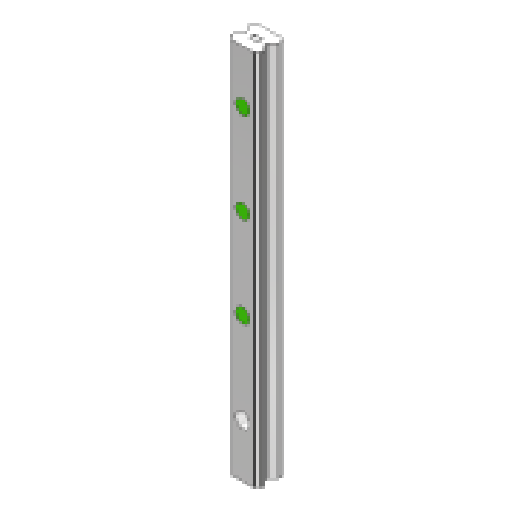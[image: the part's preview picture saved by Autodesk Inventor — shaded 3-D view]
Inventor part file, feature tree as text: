
AUTODESK INVENTOR PART (.ipt)
format: ipt  version: 2024.3 (Build 283343000, 343)  size: 185,344 bytes
history: native  units: in
note: dims shown in document units (in); Inventor stores cm internally (conversion verified against a paired STEP export)
features: extrude x1, sketch x1, imported_body x1
ambient origin geometry x8: Origin, YZ Plane, XZ Plane, XY Plane, X Axis, Y Axis, Z Axis, Center Point
bodies: Solid1 (feature_tree)
feature tree (3):
  extrude  "Extrusion1"  [1 undecoded]
  sketch  "Sketch1"  dims[d0=0.0438in d1=0.0in]
  imported_body  "Base1"
note: 1 required parameter value undecoded (feature->parameter linkage not recoverable at this tier; creation-order binding heuristic only, values carry confidence <= 0.55)
